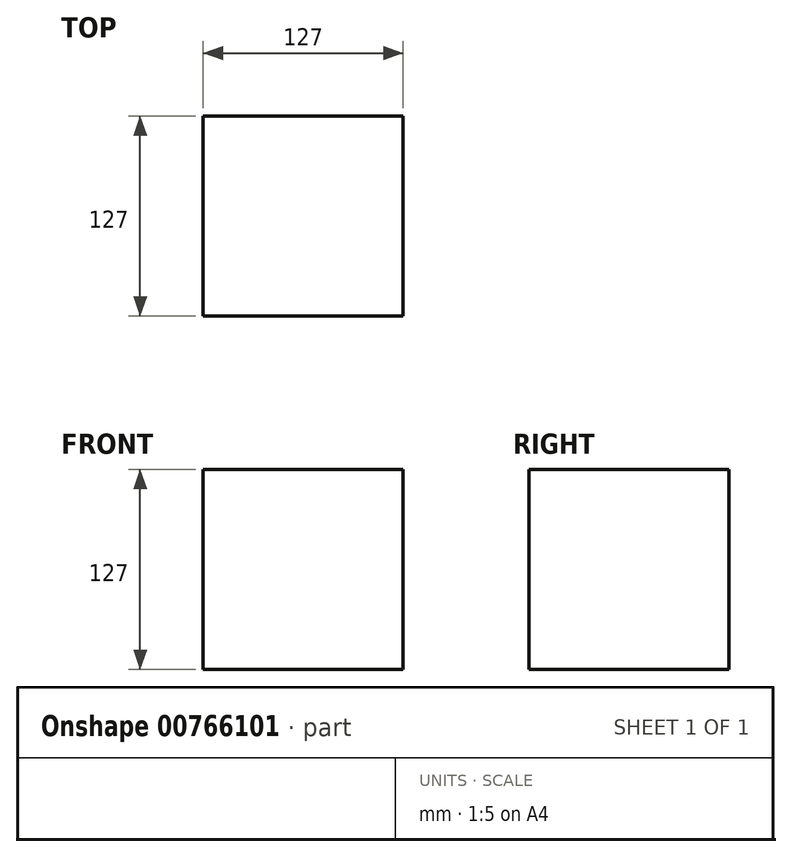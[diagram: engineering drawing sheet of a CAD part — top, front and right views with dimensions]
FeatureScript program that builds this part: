
annotation { "Feature Type Name" : "Feature", "Feature Type Description" : "" }
export const myFeature = defineFeature(function(context is Context, id is Id, definition is map)
    precondition{}
    {
        {
            var Q0;
            Q0=qCreatedBy(makeId("Front.planeOp"),FACE);
            var sketch = newSketch(context, id + "F0", { "sketchPlane" : qUnion([Q0])});
            skLineSegment(sketch, "E0.bottom", {"start": v(-45.57, -37.75) * mm, "end": v(81.43, -37.75) * mm});
            skLineSegment(sketch, "E0.top", {"start": v(-45.57, 89.25) * mm, "end": v(81.43, 89.25) * mm});
            skLineSegment(sketch, "E0.left", {"start": v(-45.57, -37.75) * mm, "end": v(-45.57, 89.25) * mm});
            skLineSegment(sketch, "E0.right", {"start": v(81.43, -37.75) * mm, "end": v(81.43, 89.25) * mm});
            skSolve(sketch);
        }
        {
            var Q0;
            Q0 = qSketchRegion(id + "F0", true);
            extrude(context, id + "F1", {"entities" : qUnion([Q0]), "depth" : 127 * mm, "offsetDistance" : 25.4 * mm});
        }
    });
